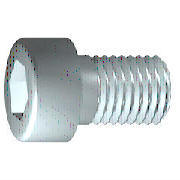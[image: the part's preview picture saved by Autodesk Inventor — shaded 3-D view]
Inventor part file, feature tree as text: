
AUTODESK INVENTOR PART (.ipt)
format: ipt  version: 2024.2 (Build 282272000, 272)  size: 198,144 bytes
history: native  units: mm (DEFAULTED — no unit token found)
features: extrude x1, plane x1, fillet x1
ambient origin geometry x7: Origin, YZ Plane, XY Plane, X Axis, Y Axis, Z Axis, Center Point
bodies: Solid1 (feature_tree), Body (feature_tree)
feature tree (3):
  extrude  "Slot"  Depth=7.0mm
  plane  "Work Plane1"
  fillet  "Fillet2"  Radius=0.24548mm
